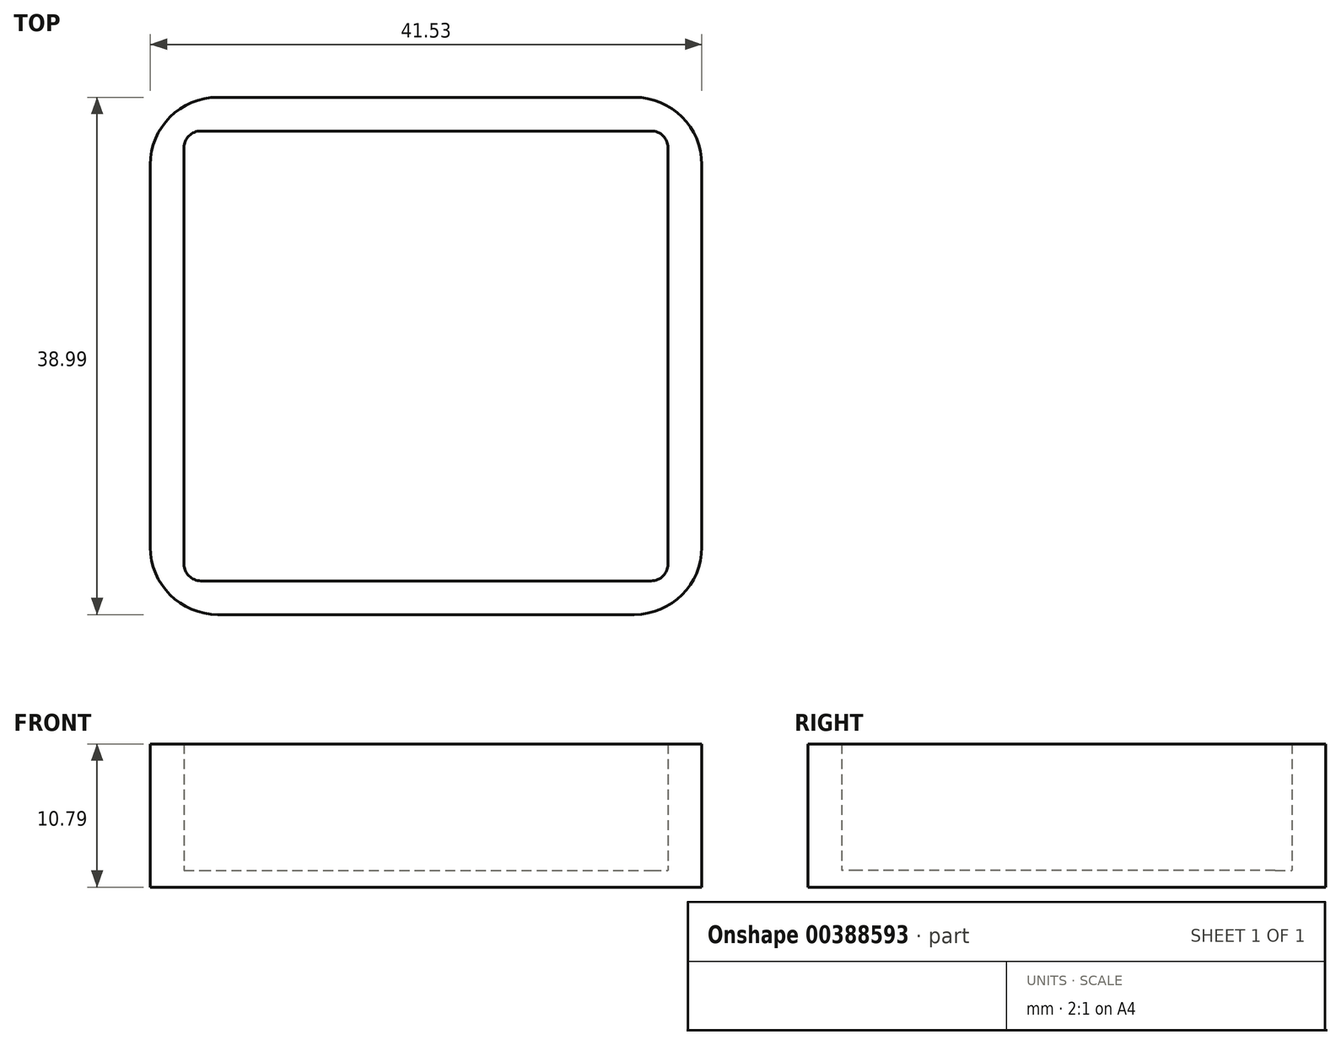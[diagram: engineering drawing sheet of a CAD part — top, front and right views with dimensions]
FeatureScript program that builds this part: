
annotation { "Feature Type Name" : "Feature", "Feature Type Description" : "" }
export const myFeature = defineFeature(function(context is Context, id is Id, definition is map)
    precondition{}
    {
        {
            var Q0;
            Q0=qCreatedBy(makeId("Top.planeOp"),FACE);
            var sketch = newSketch(context, id + "F0", { "sketchPlane" : qUnion([Q0])});
            skLineSegment(sketch, "E0.bottom", {"start": v(-18.78, 24.31) * mm, "end": v(22.75, 24.31) * mm});
            skLineSegment(sketch, "E0.top", {"start": v(-18.78, -14.68) * mm, "end": v(22.75, -14.68) * mm});
            skLineSegment(sketch, "E0.left", {"start": v(-18.78, 24.31) * mm, "end": v(-18.78, -14.68) * mm});
            skLineSegment(sketch, "E0.right", {"start": v(22.75, 24.31) * mm, "end": v(22.75, -14.68) * mm});
            skSolve(sketch);
        }
        {
            var Q0;
            Q0=makeQuery(id+"F0.imprint","IMPRINT",FACE,{"disambiguationData":[TD([[makeQuery(id+"F0.imprint","IMPRINT",EDGE,{"derivedFrom":sQuery(id+"F0.wireOp",EDGE,"E0.bottom")}),-1.0]])]});
            extrude(context, id + "F1", {"entities" : qUnion([Q0]), "depth" : 1.27 * mm});
        }
        {
            var Q0;
            Q0=makeQuery(id+"F1.opExtrude","CAP_FACE",FACE,{"disambiguationData":[OSD([sQuery(id+"F0.wireOp",EDGE,"E0.bottom"),sQuery(id+"F0.wireOp",EDGE,"E0.top"),sQuery(id+"F0.wireOp",EDGE,"E0.left"),sQuery(id+"F0.wireOp",EDGE,"E0.right")])],"isStart":false});
            var sketch = newSketch(context, id + "F2", { "sketchPlane" : qUnion([Q0])});
            skLineSegment(sketch, "E1.bottom", {"start": v(-18.78, 24.31) * mm, "end": v(22.75, 24.31) * mm});
            skLineSegment(sketch, "E1.top", {"start": v(-18.78, -14.68) * mm, "end": v(22.75, -14.68) * mm});
            skLineSegment(sketch, "E1.left", {"start": v(-18.78, 24.31) * mm, "end": v(-18.78, -14.68) * mm});
            skLineSegment(sketch, "E1.right", {"start": v(22.75, 24.31) * mm, "end": v(22.75, -14.68) * mm});
            skLineSegment(sketch, "E2.bottom", {"start": v(-16.24, 21.77) * mm, "end": v(20.2, 21.77) * mm});
            skLineSegment(sketch, "E2.top", {"start": v(-16.24, -12.14) * mm, "end": v(20.2, -12.14) * mm});
            skLineSegment(sketch, "E2.left", {"start": v(-16.24, 21.77) * mm, "end": v(-16.24, -12.14) * mm});
            skLineSegment(sketch, "E2.right", {"start": v(20.2, 21.77) * mm, "end": v(20.2, -12.14) * mm});
            skSolve(sketch);
        }
        {
            var Q0;
            Q0=makeQuery(id+"F2.imprint","IMPRINT",FACE,{"disambiguationData":[TD([[makeQuery(id+"F2.imprint","IMPRINT",EDGE,{"derivedFrom":sQuery(id+"F2.wireOp",EDGE,"E1.bottom")}),-1.0]])]});
            extrude(context, id + "F3", {"entities" : qUnion([Q0]), "operationType" : NewBodyOperationType.ADD, "depth" : 9.52 * mm});
        }
        {
            var Q0;
            Q0=makeQuery(id+"F3.boolean.opBoolean","MERGE",EDGE,{"derivedFrom":[makeQuery(id+"F1.opExtrude","SWEPT_EDGE",EDGE,{"disambiguationData":[OSD([sQuery(id+"F0.wireOp",EDGE,"E0.bottom"),sQuery(id+"F0.wireOp",EDGE,"E0.left")])]}),makeQuery(id+"F3.opExtrude","SWEPT_EDGE",EDGE,{"disambiguationData":[OSD([sQuery(id+"F2.wireOp",EDGE,"E1.bottom"),sQuery(id+"F2.wireOp",EDGE,"E1.left")])]})]});
            var Q1;
            Q1=makeQuery(id+"F3.boolean.opBoolean","MERGE",EDGE,{"derivedFrom":[makeQuery(id+"F1.opExtrude","SWEPT_EDGE",EDGE,{"disambiguationData":[OSD([sQuery(id+"F0.wireOp",EDGE,"E0.bottom"),sQuery(id+"F0.wireOp",EDGE,"E0.right")])]}),makeQuery(id+"F3.opExtrude","SWEPT_EDGE",EDGE,{"disambiguationData":[OSD([sQuery(id+"F2.wireOp",EDGE,"E1.bottom"),sQuery(id+"F2.wireOp",EDGE,"E1.right")])]})]});
            var Q2;
            Q2=makeQuery(id+"F3.boolean.opBoolean","MERGE",EDGE,{"derivedFrom":[makeQuery(id+"F1.opExtrude","SWEPT_EDGE",EDGE,{"disambiguationData":[OSD([sQuery(id+"F0.wireOp",EDGE,"E0.top"),sQuery(id+"F0.wireOp",EDGE,"E0.right")])]}),makeQuery(id+"F3.opExtrude","SWEPT_EDGE",EDGE,{"disambiguationData":[OSD([sQuery(id+"F2.wireOp",EDGE,"E1.top"),sQuery(id+"F2.wireOp",EDGE,"E1.right")])]})]});
            var Q3;
            Q3=makeQuery(id+"F3.boolean.opBoolean","MERGE",EDGE,{"derivedFrom":[makeQuery(id+"F1.opExtrude","SWEPT_EDGE",EDGE,{"disambiguationData":[OSD([sQuery(id+"F0.wireOp",EDGE,"E0.top"),sQuery(id+"F0.wireOp",EDGE,"E0.left")])]}),makeQuery(id+"F3.opExtrude","SWEPT_EDGE",EDGE,{"disambiguationData":[OSD([sQuery(id+"F2.wireOp",EDGE,"E1.top"),sQuery(id+"F2.wireOp",EDGE,"E1.left")])]})]});
            fillet(context, id + "F4", {"entities" : qUnion([Q0, Q1, Q2, Q3]), "radius" : 5.08 * mm, "tangentPropagation" : true, "allowEdgeOverflow" : false});
        }
        {
            var Q0;
            Q0=makeQuery(id+"F3.opExtrude","SWEPT_EDGE",EDGE,{"disambiguationData":[OSD([sQuery(id+"F2.wireOp",EDGE,"E2.bottom"),sQuery(id+"F2.wireOp",EDGE,"E2.left")])]});
            var Q1;
            Q1=makeQuery(id+"F3.opExtrude","SWEPT_EDGE",EDGE,{"disambiguationData":[OSD([sQuery(id+"F2.wireOp",EDGE,"E2.bottom"),sQuery(id+"F2.wireOp",EDGE,"E2.right")])]});
            var Q2;
            Q2=makeQuery(id+"F3.opExtrude","SWEPT_EDGE",EDGE,{"disambiguationData":[OSD([sQuery(id+"F2.wireOp",EDGE,"E2.top"),sQuery(id+"F2.wireOp",EDGE,"E2.right")])]});
            var Q3;
            Q3=makeQuery(id+"F3.opExtrude","SWEPT_EDGE",EDGE,{"disambiguationData":[OSD([sQuery(id+"F2.wireOp",EDGE,"E2.top"),sQuery(id+"F2.wireOp",EDGE,"E2.left")])]});
            fillet(context, id + "F5", {"entities" : qUnion([Q0, Q1, Q2, Q3]), "radius" : 1.27 * mm, "tangentPropagation" : true, "allowEdgeOverflow" : false});
        }
    });
